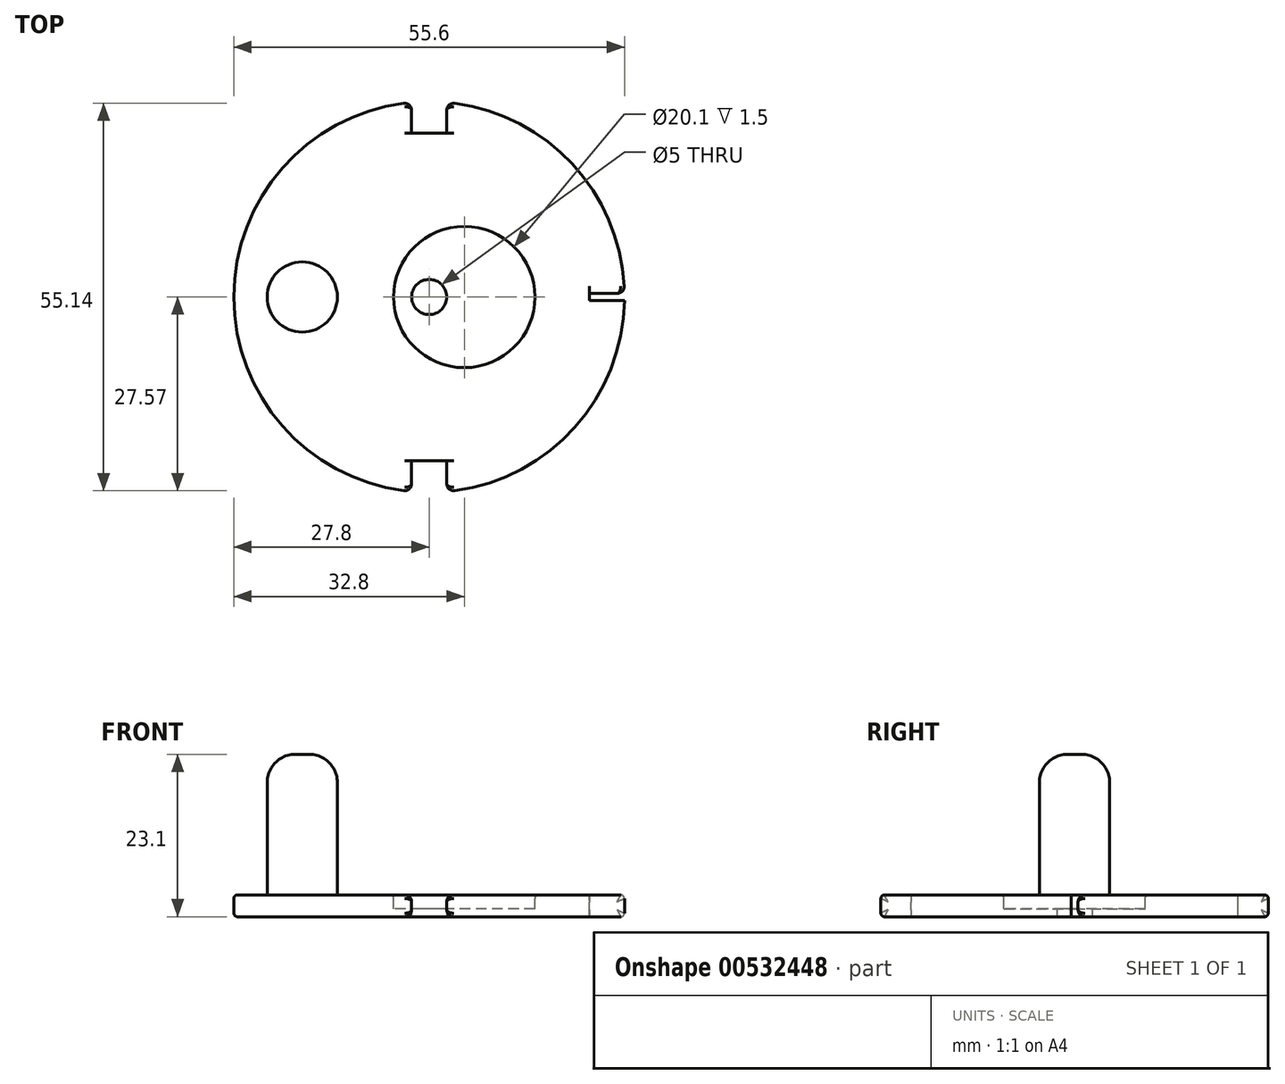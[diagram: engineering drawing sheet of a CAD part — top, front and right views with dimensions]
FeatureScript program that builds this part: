
annotation { "Feature Type Name" : "Feature", "Feature Type Description" : "" }
export const myFeature = defineFeature(function(context is Context, id is Id, definition is map)
    precondition{}
    {
        {
            var Q0;
            Q0=qCreatedBy(makeId("Top.planeOp"),FACE);
            var sketch = newSketch(context, id + "F0", { "sketchPlane" : qUnion([Q0])});
            skCircle(sketch, "E0", {"center": v(0, 0) * mm, "radius": 27.8 * mm});
            skSolve(sketch);
        }
        {
            var Q0;
            Q0=qSketchRegion(id+"F0",true);
            extrude(context, id + "F1", {"entities" : qUnion([Q0]), "depth" : 3.1 * mm});
        }
        {
            var Q0;
            Q0=makeQuery(id+"F1.opExtrude","CAP_FACE",FACE,{"disambiguationData":[OSD([sQuery(id+"F0.wireOp",EDGE,"E0")])],"isStart":false});
            var sketch = newSketch(context, id + "F2", { "sketchPlane" : qUnion([Q0])});
            skCircle(sketch, "E1", {"center": v(5, 0) * mm, "radius": 10.05 * mm});
            skSolve(sketch);
        }
        {
            var Q0;
            Q0=qSketchRegion(id+"F2",true);
            extrude(context, id + "F3", {"entities" : qUnion([Q0]), "operationType" : NewBodyOperationType.REMOVE, "oppositeDirection" : true, "depth" : 2 * mm});
        }
        {
            var Q0;
            Q0=makeQuery(id+"F1.opExtrude","CAP_FACE",FACE,{"disambiguationData":[OSD([sQuery(id+"F0.wireOp",EDGE,"E0")])],"isStart":false});
            var Q1;
            Q1=makeQuery(id+"F1.opExtrude","CAP_FACE",FACE,{"disambiguationData":[OSD([sQuery(id+"F0.wireOp",EDGE,"E0")])],"isStart":true});
            fillet(context, id + "F4", {"entities" : qUnion([Q0, Q1]), "radius" : 0.5 * mm, "tangentPropagation" : true, "allowEdgeOverflow" : false});
        }
        {
            var Q0;
            Q0=makeQuery(id+"F1.opExtrude","CAP_FACE",FACE,{"disambiguationData":[OSD([sQuery(id+"F0.wireOp",EDGE,"E0")])],"isStart":true});
            var sketch = newSketch(context, id + "F5", { "sketchPlane" : qUnion([Q0])});
            skCircle(sketch, "E2", {"center": v(0, 0) * mm, "radius": 2.5 * mm});
            skSolve(sketch);
        }
        {
            var Q0;
            Q0=qSketchRegion(id+"F5",true);
            extrude(context, id + "F6", {"entities" : qUnion([Q0]), "operationType" : NewBodyOperationType.REMOVE, "endBound" : BoundingType.THROUGH_ALL, "oppositeDirection" : true, "depth" : 25 * mm});
        }
        {
            var Q0;
            Q0=makeQuery(id+"F1.opExtrude","CAP_FACE",FACE,{"disambiguationData":[OSD([sQuery(id+"F0.wireOp",EDGE,"E0")])],"isStart":false});
            var sketch = newSketch(context, id + "F7", { "sketchPlane" : qUnion([Q0])});
            skLineSegment(sketch, "E3.bottom", {"start": v(-2.5, 28.3) * mm, "end": v(2.5, 28.3) * mm});
            skLineSegment(sketch, "E3.top", {"start": v(-2.5, 23.3) * mm, "end": v(2.5, 23.3) * mm});
            skLineSegment(sketch, "E3.left", {"start": v(-2.5, 28.3) * mm, "end": v(-2.5, 23.3) * mm});
            skLineSegment(sketch, "E3.right", {"start": v(2.5, 28.3) * mm, "end": v(2.5, 23.3) * mm});
            skPoint(sketch, "E3.middle", {"position": v(0, 25.8) * mm});
            skLineSegment(sketch, "E4.MirrorCS", {"start": v(-2.5, -23.3) * mm, "end": v(2.5, -23.3) * mm});
            skLineSegment(sketch, "E5.MirrorCS", {"start": v(-2.5, -28.3) * mm, "end": v(2.5, -28.3) * mm});
            skLineSegment(sketch, "E6.MirrorCS", {"start": v(-2.5, -28.3) * mm, "end": v(-2.5, -23.3) * mm});
            skPoint(sketch, "E7.MirrorP", {"position": v(0, -25.8) * mm});
            skLineSegment(sketch, "E8.MirrorCS", {"start": v(2.5, -28.3) * mm, "end": v(2.5, -23.3) * mm});
            skSolve(sketch);
        }
        {
            var Q0;
            Q0=qSketchRegion(id+"F7",true);
            extrude(context, id + "F8", {"entities" : qUnion([Q0]), "operationType" : NewBodyOperationType.REMOVE, "endBound" : BoundingType.THROUGH_ALL, "oppositeDirection" : true, "depth" : 25 * mm, "offsetDistance" : 25 * mm});
        }
        {
            var Q0;
            Q0=makeQuery(id+"F8.boolean.opBoolean","INTERSECT",EDGE,{"derivedFrom":[makeQuery(id+"F1.opExtrude","SWEPT_FACE",FACE,{"disambiguationData":[OSD([sQuery(id+"F0.wireOp",EDGE,"E0")])]}),makeQuery(id+"F8.opExtrude","SWEPT_FACE",FACE,{"disambiguationData":[OSD([sQuery(id+"F7.wireOp",EDGE,"E6.MirrorCS")])]})]});
            var Q1;
            Q1=makeQuery(id+"F8.boolean.opBoolean","INTERSECT",EDGE,{"derivedFrom":[makeQuery(id+"F1.opExtrude","SWEPT_FACE",FACE,{"disambiguationData":[OSD([sQuery(id+"F0.wireOp",EDGE,"E0")])]}),makeQuery(id+"F8.opExtrude","SWEPT_FACE",FACE,{"disambiguationData":[OSD([sQuery(id+"F7.wireOp",EDGE,"E8.MirrorCS")])]})]});
            var Q2;
            Q2=makeQuery(id+"F8.boolean.opBoolean","INTERSECT",EDGE,{"derivedFrom":[makeQuery(id+"F1.opExtrude","SWEPT_FACE",FACE,{"disambiguationData":[OSD([sQuery(id+"F0.wireOp",EDGE,"E0")])]}),makeQuery(id+"F8.opExtrude","SWEPT_FACE",FACE,{"disambiguationData":[OSD([sQuery(id+"F7.wireOp",EDGE,"E3.left")])]})]});
            var Q3;
            Q3=makeQuery(id+"F8.boolean.opBoolean","INTERSECT",EDGE,{"derivedFrom":[makeQuery(id+"F1.opExtrude","SWEPT_FACE",FACE,{"disambiguationData":[OSD([sQuery(id+"F0.wireOp",EDGE,"E0")])]}),makeQuery(id+"F8.opExtrude","SWEPT_FACE",FACE,{"disambiguationData":[OSD([sQuery(id+"F7.wireOp",EDGE,"E3.right")])]})]});
            fillet(context, id + "F9", {"entities" : qUnion([Q0, Q1, Q2, Q3]), "radius" : 1 * mm, "tangentPropagation" : true, "allowEdgeOverflow" : false});
        }
        {
            var Q0;
            Q0=makeQuery(id+"F1.opExtrude","CAP_FACE",FACE,{"disambiguationData":[OSD([sQuery(id+"F0.wireOp",EDGE,"E0")])],"isStart":false});
            var sketch = newSketch(context, id + "F10", { "sketchPlane" : qUnion([Q0])});
            skCircle(sketch, "E9", {"center": v(-18.07, 0) * mm, "radius": 5 * mm});
            skSolve(sketch);
        }
        {
            var Q0;
            Q0 = qSketchRegion(id + "F10", true);
            extrude(context, id + "F11", {"entities" : qUnion([Q0]), "operationType" : NewBodyOperationType.ADD, "depth" : 20 * mm, "offsetDistance" : 25 * mm});
        }
        {
            var Q0;
            Q0=makeQuery(id+"F11.opExtrude","CAP_FACE",FACE,{"disambiguationData":[OSD([sQuery(id+"F10.wireOp",EDGE,"E9")])],"isStart":false});
            var Q1;
            Q1=makeQuery(id+"F11.opExtrude","CAP_EDGE",EDGE,{"disambiguationData":[OSD([sQuery(id+"F10.wireOp",EDGE,"E9")])],"isStart":true});
            fillet(context, id + "F12", {"entities" : qUnion([Q0, Q1]), "radius" : 4 * mm, "tangentPropagation" : true, "allowEdgeOverflow" : false});
        }
        {
            var Q0;
            Q0=makeQuery(id+"F1.opExtrude","CAP_FACE",FACE,{"disambiguationData":[OSD([sQuery(id+"F0.wireOp",EDGE,"E0")])],"isStart":false});
            var sketch = newSketch(context, id + "F13", { "sketchPlane" : qUnion([Q0])});
            skLineSegment(sketch, "E10.bottom", {"start": v(27.8, -0.5) * mm, "end": v(22.8, -0.5) * mm});
            skLineSegment(sketch, "E10.top", {"start": v(27.8, 0.5) * mm, "end": v(22.8, 0.5) * mm});
            skLineSegment(sketch, "E10.left", {"start": v(27.8, -0.5) * mm, "end": v(27.8, 0.5) * mm});
            skLineSegment(sketch, "E10.right", {"start": v(22.8, -0.5) * mm, "end": v(22.8, 0.5) * mm});
            skPoint(sketch, "E10.middle", {"position": v(25.3, 0) * mm});
            skPoint(sketch, "E10.middle.positionSnap0", {"position": v(27.3, 0) * mm});
            skPoint(sketch, "E10.centerSnap0", {"position": v(27.3, 0) * mm});
            skSolve(sketch);
        }
        {
            var Q0;
            {var subQ0=sQuery(id+"F13.wireOp",EDGE,"E10.right");Q0=makeQuery(id+"F13.imprint","IMPRINT",FACE,{"disambiguationData":[TD([[makeQuery(id+"F13.imprint","IMPRINT",EDGE,{"derivedFrom":subQ0}),-1.0]])]});}
            var Q1;
            Q1 = qSketchRegion(id + "F13", true);
            extrude(context, id + "F14", {"entities" : qUnion([Q0, Q1]), "operationType" : NewBodyOperationType.REMOVE, "endBound" : BoundingType.THROUGH_ALL, "oppositeDirection" : true, "depth" : 25 * mm, "offsetDistance" : 25 * mm});
        }
        {
            var Q0;
            Q0=makeQuery(id+"F14.boolean.opBoolean","COPY",EDGE,{"derivedFrom":makeQuery(id+"F14.opExtrude","SWEPT_EDGE",EDGE,{"disambiguationData":[OSD([sQuery(id+"F13.wireOp",EDGE,"E10.top"),sQuery(id+"F13.wireOp",EDGE,"E10.left")])]})});
            var Q1;
            Q1=makeQuery(id+"F14.boolean.opBoolean","COPY",EDGE,{"derivedFrom":makeQuery(id+"F14.opExtrude","SWEPT_EDGE",EDGE,{"disambiguationData":[OSD([sQuery(id+"F13.wireOp",EDGE,"E10.bottom"),sQuery(id+"F13.wireOp",EDGE,"E10.left")])]})});
            fillet(context, id + "F15", {"entities" : qUnion([Q0, Q1]), "radius" : 1 * mm, "tangentPropagation" : true, "allowEdgeOverflow" : false});
        }
    });
